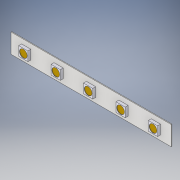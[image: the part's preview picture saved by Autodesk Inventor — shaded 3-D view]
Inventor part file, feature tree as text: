
AUTODESK INVENTOR PART (.ipt)
format: ipt  version: 2019 (Build 230136000, 136)  size: 156,160 bytes
history: native  units: mm
features: extrude x3, sketch x3, pattern_linear x1
ambient origin geometry x8: Origin, YZ Plane, XZ Plane, XY Plane, X Axis, Y Axis, Z Axis, Center Point
bodies: Solid1 (feature_tree)
feature tree (7):
  extrude  "Extrusion1"  Depth=10.0mm
  extrude  "Extrusion2"  Depth=4.8mm
  extrude  "Extrusion3"  Depth=5.5mm
  pattern_linear  "Rectangular Pattern1"  Count1=5 Spacing1=16.8mm
  sketch  "Sketch1"  dims[d0=83.0mm d1=10.0mm]
  sketch  "Sketch2"  dims[d2=0.4mm d3=0.0mm d4=4.8mm]
  sketch  "Sketch3"  dims[d5=4.8mm d6=5.5mm d7=50.0mm d9=16.8mm d10=10.0mm d12=10.0mm d14=1.5mm d15=0.0mm d16=4.0mm d17=0.2mm d18=0.0mm d19=50.0mm d21=16.8mm]
